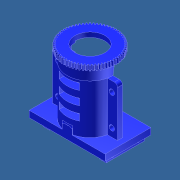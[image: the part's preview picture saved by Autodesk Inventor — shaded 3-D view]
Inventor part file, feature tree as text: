
AUTODESK INVENTOR PART (.ipt)
format: ipt  version: Autodesk Inventor 2014  size: 1,054,208 bytes
history: native  units: in
note: dims shown in document units (in); Inventor stores cm internally (conversion verified against a paired STEP export)
features: sketch x7, extrude x5, imported_body x1, fillet x1, hole x1
ambient origin geometry x8: Origin, YZ Plane, XZ Plane, XY Plane, X Axis, Y Axis, Z Axis, Center Point
feature tree (15):
  imported_body  "Base1"
  extrude  "Extrusion1"  Depth=0.25in TaperAngle=0.0deg
  extrude  "Extrusion2"  Depth=0.125in
  fillet  "Fillet1"  Radius=0.25in
  extrude  "Extrusion3"  Depth=0.25in
  extrude  "Extrusion4"  Depth=1.5in
  extrude  "Extrusion5"  Depth=0.25in
  hole  "Hole2"  [1 undecoded]
  sketch  "Sketch8"  dims[d33=0.1625in d34=0.1625in d35=0.25in d36=1.0in d37=0.201in d38=0.75in d39=0.385in d40=0.25in d41=0.5635in d42=1.0in d43=0.8108in]
  sketch  "Sketch1"  dims[d0=0.1125in d1=0.25in d2=0.0in]
  sketch  "Sketch3"  dims[d18=0.25in d19=0.0in d20=0.125in d21=0.25in d22=0.0in]
  sketch  "Sketch4"  dims[d23=0.5in d24=0.0in d25=0.25in]
  sketch  "Sketch5"  dims[d26=0.25in d27=1.5in]
  sketch  "Sketch6"  dims[d28=0.25in d29=0.25in]
  sketch  "Sketch7"  dims[d30=1.5in d31=0.325in d32=0.0in]
note: 1 required parameter value undecoded (feature->parameter linkage not recoverable at this tier; creation-order binding heuristic only, values carry confidence <= 0.55)
